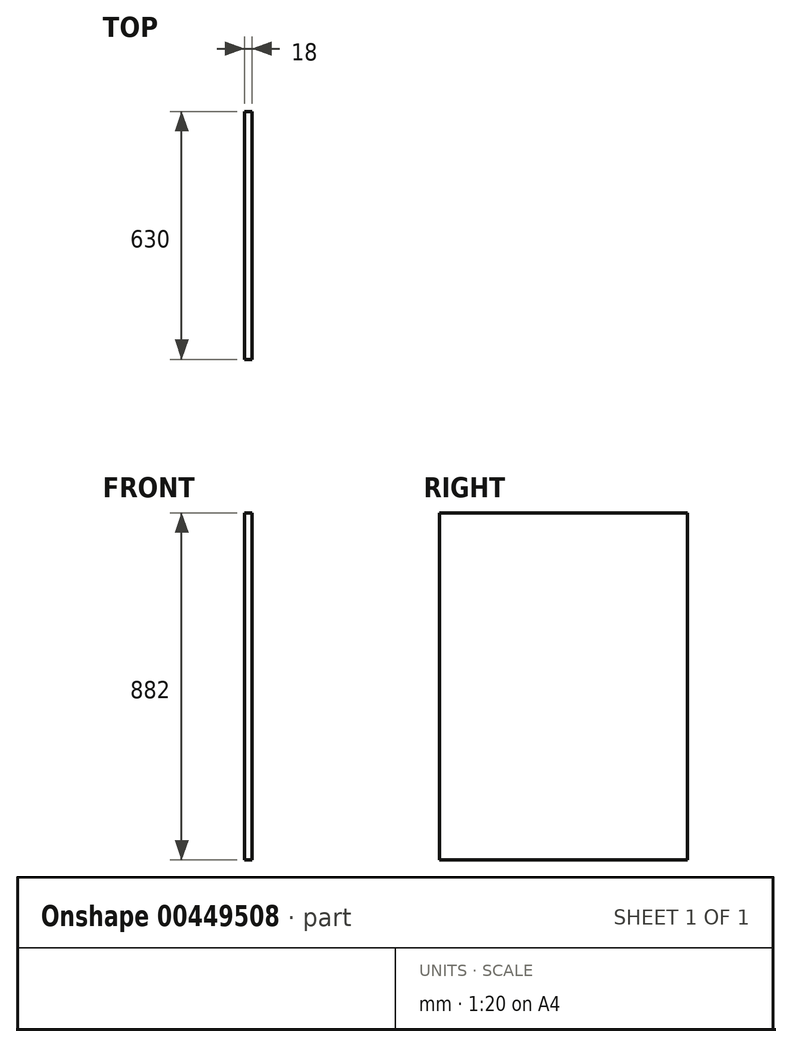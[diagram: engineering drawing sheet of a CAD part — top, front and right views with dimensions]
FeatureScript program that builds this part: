
annotation { "Feature Type Name" : "Feature", "Feature Type Description" : "" }
export const myFeature = defineFeature(function(context is Context, id is Id, definition is map)
    precondition{}
    {
        {
            var Q0;
            Q0=qCreatedBy(makeId("Right.planeOp"),FACE);
            var sketch = newSketch(context, id + "F0", { "sketchPlane" : qUnion([Q0])});
            skLineSegment(sketch, "E0.bottom", {"start": v(0, 882) * mm, "end": v(630, 882) * mm});
            skLineSegment(sketch, "E0.top", {"start": v(0, 0) * mm, "end": v(630, 0) * mm});
            skLineSegment(sketch, "E0.left", {"start": v(0, 882) * mm, "end": v(0, 0) * mm});
            skLineSegment(sketch, "E0.right", {"start": v(630, 882) * mm, "end": v(630, 0) * mm});
            skSolve(sketch);
        }
        {
            var Q0;
            Q0=qSketchRegion(id+"F0",true);
            extrude(context, id + "F1", {"entities" : qUnion([Q0]), "oppositeDirection" : true, "depth" : 18 * mm});
        }
    });
